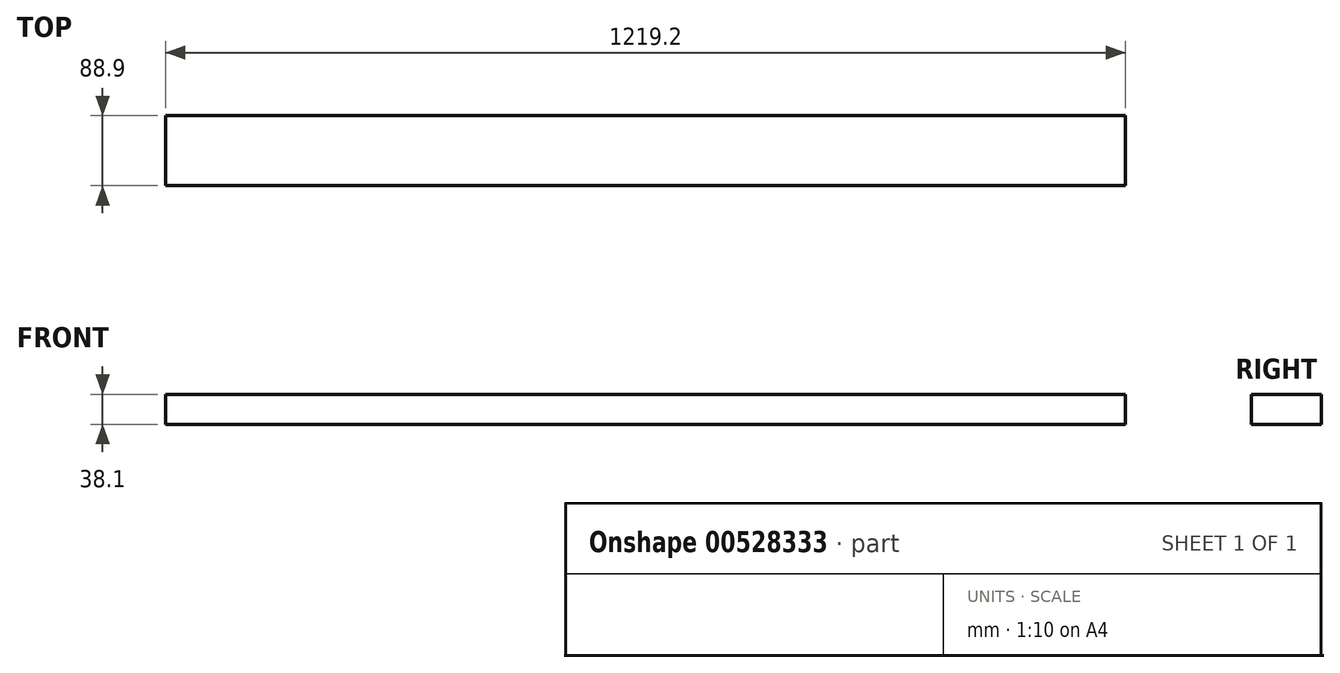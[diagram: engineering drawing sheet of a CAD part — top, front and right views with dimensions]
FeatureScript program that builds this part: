
annotation { "Feature Type Name" : "Feature", "Feature Type Description" : "" }
export const myFeature = defineFeature(function(context is Context, id is Id, definition is map)
    precondition{}
    {
        {
            var Q0;
            Q0=qCreatedBy(makeId("Front.planeOp"),FACE);
            var sketch = newSketch(context, id + "F0", { "sketchPlane" : qUnion([Q0])});
            skLineSegment(sketch, "E0", {"start": v(-1219.2, 38.1) * mm, "end": v(0, 38.1) * mm});
            skLineSegment(sketch, "E1", {"start": v(0, 38.1) * mm, "end": v(0, 0) * mm});
            skLineSegment(sketch, "E2", {"start": v(0, 0) * mm, "end": v(-1219.2, 0) * mm});
            skLineSegment(sketch, "E3", {"start": v(-1219.2, 0) * mm, "end": v(-1219.2, 38.1) * mm});
            skSolve(sketch);
        }
        {
            var Q0;
            Q0 = qSketchRegion(id + "F0", true);
            extrude(context, id + "F1", {"entities" : qUnion([Q0]), "depth" : 88.9 * mm, "offsetDistance" : 25 * mm});
        }
    });
